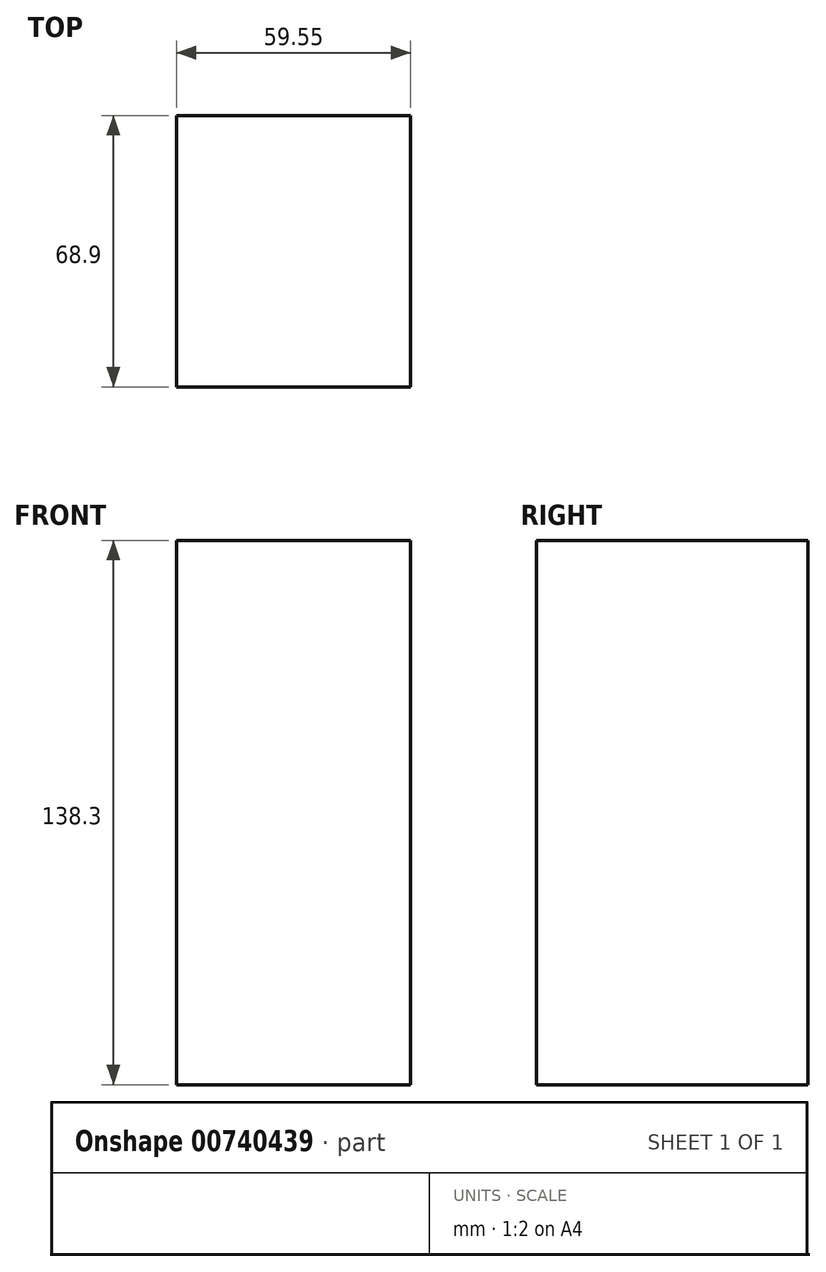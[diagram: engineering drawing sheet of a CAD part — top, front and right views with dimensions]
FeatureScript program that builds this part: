
annotation { "Feature Type Name" : "Feature", "Feature Type Description" : "" }
export const myFeature = defineFeature(function(context is Context, id is Id, definition is map)
    precondition{}
    {
        {
            var Q0;
            Q0=qCreatedBy(makeId("Top.planeOp"),FACE);
            var sketch = newSketch(context, id + "F0", { "sketchPlane" : qUnion([Q0])});
            skLineSegment(sketch, "E0.bottom", {"start": v(-42.01, -42.46) * mm, "end": v(17.54, -42.46) * mm});
            skLineSegment(sketch, "E0.top", {"start": v(-42.01, 26.44) * mm, "end": v(17.54, 26.44) * mm});
            skLineSegment(sketch, "E0.left", {"start": v(-42.01, -42.46) * mm, "end": v(-42.01, 26.44) * mm});
            skLineSegment(sketch, "E0.right", {"start": v(17.54, -42.46) * mm, "end": v(17.54, 26.44) * mm});
            skSolve(sketch);
        }
        {
            var Q0;
            Q0 = qSketchRegion(id + "F0", true);
            extrude(context, id + "F1", {"entities" : qUnion([Q0]), "depth" : 138.3 * mm, "offsetDistance" : 25 * mm});
        }
    });
